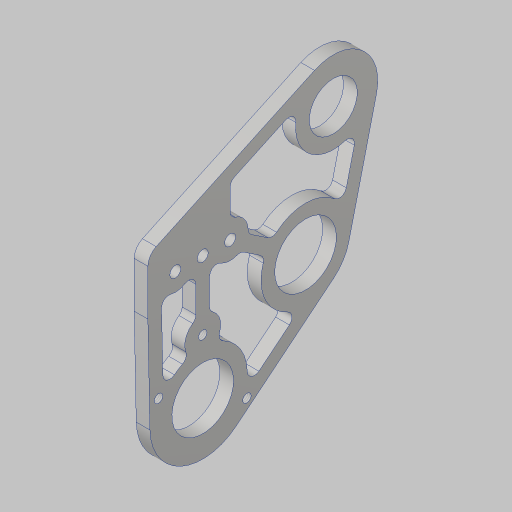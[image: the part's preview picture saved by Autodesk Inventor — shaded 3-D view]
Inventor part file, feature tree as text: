
AUTODESK INVENTOR PART (.ipt)
format: ipt  version: 2023.5 (Build 275446000, 446)  size: 314,368 bytes
history: native  units: in
note: dims shown in document units (in); Inventor stores cm internally (conversion verified against a paired STEP export)
features: sketch x3, extrude x2, hole x2, fillet x2, projected_geometry x2
ambient origin geometry x8: Origin, YZ Plane, XZ Plane, XY Plane, X Axis, Y Axis, Z Axis, Center Point
bodies: Solid1 (feature_tree)
feature tree (11):
  sketch  "Sketch1"  dims[d0=1.0in d1=2.0in]
  extrude  "Extrusion1"  Depth=2.0in
  hole  "Hole1"  [1 undecoded]
  hole  "Hole3"  [1 undecoded]
  extrude  "Extrusion2"  Depth=0.26in
  fillet  "Fillet1"  Radius=0.5in
  fillet  "Fillet2"  Radius=0.5in
  sketch  "Sketch2"  dims[d2=1.125in d3=2.25in]
  sketch  "Sketch3"  dims[d4=3.0in d5=5.0in d6=1.949in d11=0.5in d12=0.5in d13=0.4in d18=0.4688in d19=2.5in d20=1.375in d21=1.74in d22=8.0in d23=1.0in d24=2.1066in d25=0.25in d26=0.0in d29=2.3622in d31=360.0deg d33=0.201in d34=0.75in d35=0.385in d36=0.25in d37=0.5635in d38=1.0in d39=0.8108in d40=1.0in d41=3.3in d42=1.6in d43=3.0in d44=1.4348in d46=0.25in d48=0.5in d49=1.0in d50=0.875in d51=1.25in d52=0.75in d54=0.125in d62=0.875in d63=1.0in d64=0.156in d65=0.38in d66=0.385in d67=0.25in d68=0.5635in d69=1.0in d70=0.8108in d71=0.25in d72=0.25in d73=0.25in d74=0.25in d75=0.125in d76=0.125in d77=0.125in d78=0.125in d79=0.0in d80=0.0in d81=0.13in d82=0.26in d83=1.8in d84=0.4in]
  projected_geometry  "Project Cut Edges1"
  projected_geometry  "Project Cut Edges2"
note: 2 required parameter values undecoded (feature->parameter linkage not recoverable at this tier; creation-order binding heuristic only, values carry confidence <= 0.55)
